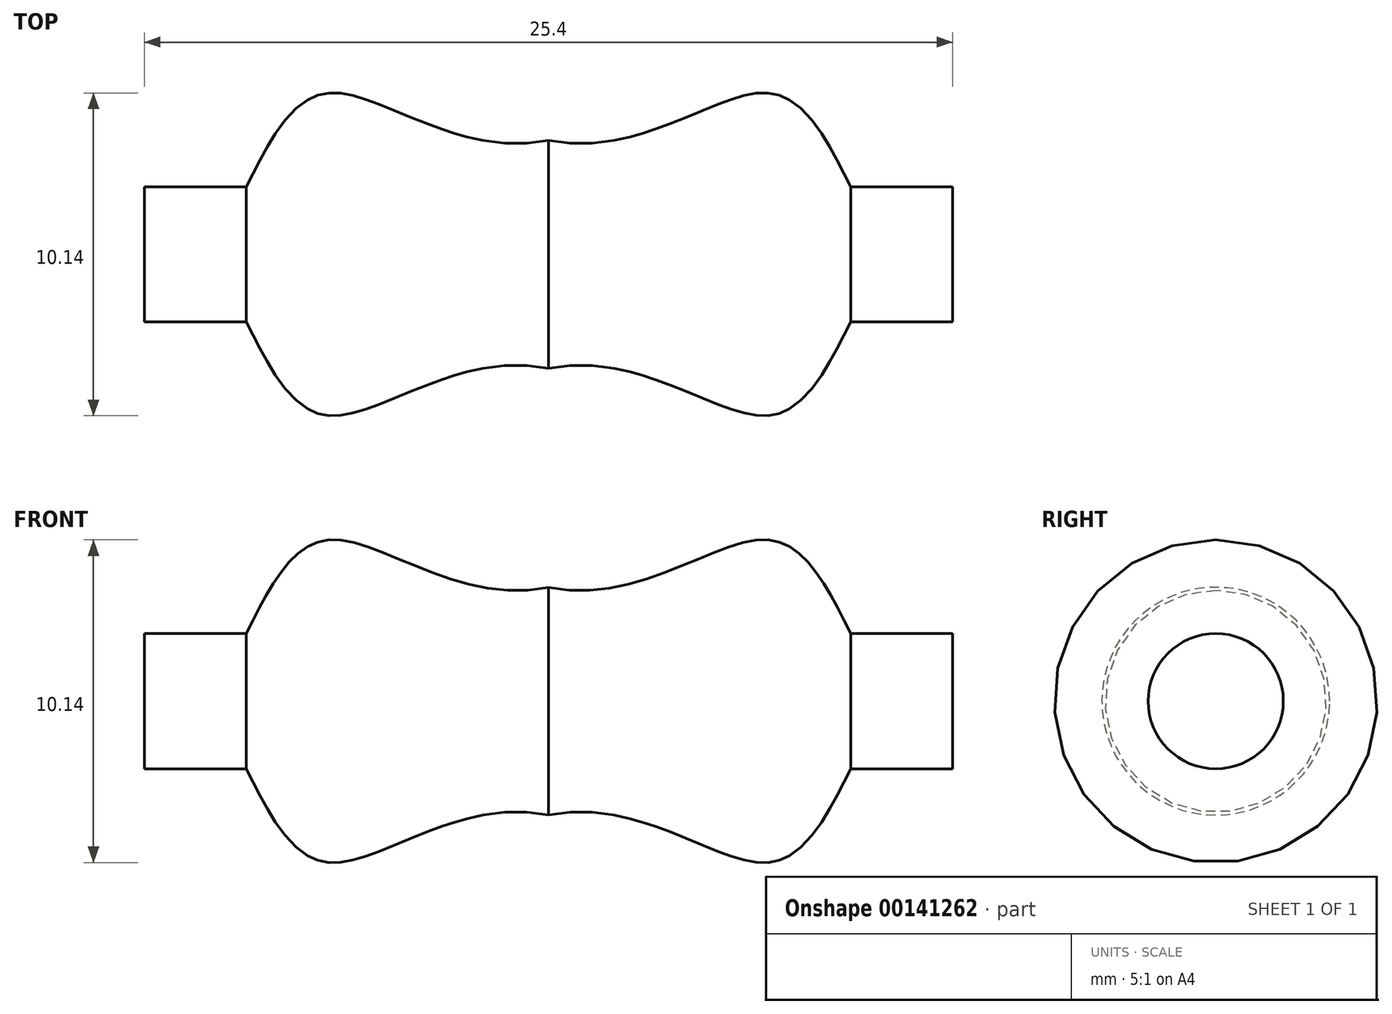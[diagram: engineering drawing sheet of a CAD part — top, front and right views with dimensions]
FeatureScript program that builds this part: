
annotation { "Feature Type Name" : "Feature", "Feature Type Description" : "" }
export const myFeature = defineFeature(function(context is Context, id is Id, definition is map)
    precondition{}
    {
        {
            var Q0;
            Q0=qCreatedBy(makeId("Front.planeOp"),FACE);
            var sketch = newSketch(context, id + "F0", { "sketchPlane" : qUnion([Q0])});
            skLineSegment(sketch, "E0", {"start": v(0, 0) * mm, "end": v(12.7, 0) * mm});
            skLineSegment(sketch, "E1", {"start": v(12.7, 0) * mm, "end": v(12.7, 2.12) * mm});
            skLineSegment(sketch, "E2", {"start": v(12.7, 2.12) * mm, "end": v(9.5, 2.12) * mm});
            skFitSpline(sketch, "E3", {"points": [v(9.5, 2.12) * mm, v(7, 5.06) * mm, v(0, 3.58) * mm], "startDerivative": vector(-4.6, 8.94) * mm, "endDerivative": vector(-15.18, 3.13) * mm});
            skFitSpline(sketch, "E4.MirrorCS", {"points": [v(-9.5, 2.12) * mm, v(-7, 5.06) * mm, v(0, 3.58) * mm], "startDerivative": vector(4.6, 8.94) * mm, "endDerivative": vector(15.18, 3.13) * mm});
            skLineSegment(sketch, "E5.MirrorCS", {"start": v(-12.7, 2.12) * mm, "end": v(-9.5, 2.12) * mm});
            skLineSegment(sketch, "E6.MirrorCS", {"start": v(-12.7, 0) * mm, "end": v(-12.7, 2.12) * mm});
            skLineSegment(sketch, "E7.MirrorCS", {"start": v(0, 0) * mm, "end": v(-12.7, 0) * mm});
            skSolve(sketch);
        }
        {
            var Q0;
            Q0=makeQuery(id+"F0.imprint","IMPRINT",FACE,{"disambiguationData":[TD([[makeQuery(id+"F0.imprint","IMPRINT",EDGE,{"derivedFrom":sQuery(id+"F0.wireOp",EDGE,"E0")}),1.0]])]});
            var sketch = newSketch(context, id + "F1", { "sketchPlane" : qUnion([Q0])});
            skLineSegment(sketch, "E8", {"start": v(-38.05, 0) * mm, "end": v(37.93, 0) * mm});
            skSolve(sketch);
        }
        {
            var Q0;
            Q0 = qSketchRegion(id + "F0", true);
            var Q1;
            Q1=sQuery(id+"F1.wireOp",EDGE,"E8");
            revolve(context, id + "F2", {"entities" : qUnion([Q0]), "axis" : qUnion([Q1]), "revolveType" : RevolveType.FULL});
        }
    });
